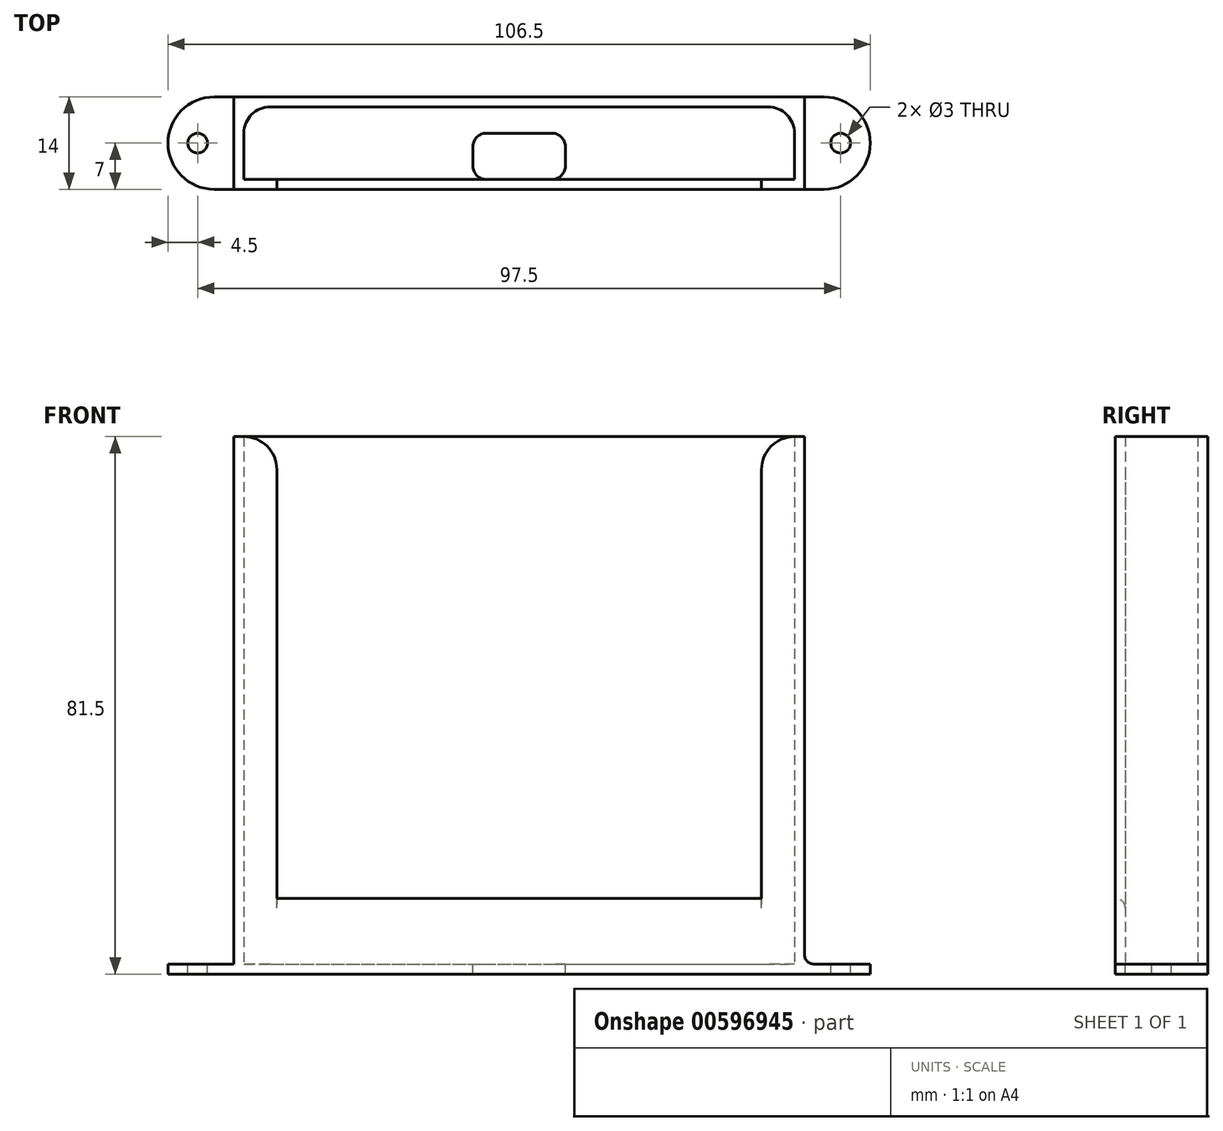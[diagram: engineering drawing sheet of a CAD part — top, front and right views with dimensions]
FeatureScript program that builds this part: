
annotation { "Feature Type Name" : "Feature", "Feature Type Description" : "" }
export const myFeature = defineFeature(function(context is Context, id is Id, definition is map)
    precondition{}
    {
        {
            assignVariable(context, id + "F0", {"name" : "THK", "anyValue" : 1.5});
        }
        {
            var Q0;
            Q0=qCreatedBy(makeId("Top.planeOp"),FACE);
            var sketch = newSketch(context, id + "F1", { "sketchPlane" : qUnion([Q0])});
            skLineSegment(sketch, "E0.bottom", {"start": v(-85, -1.5) * mm, "end": v(-1.5, -1.5) * mm});
            skLineSegment(sketch, "E0.top", {"start": v(-85, -12.5) * mm, "end": v(-1.5, -12.5) * mm});
            skLineSegment(sketch, "E0.left", {"start": v(-85, -1.5) * mm, "end": v(-85, -12.5) * mm});
            skLineSegment(sketch, "E0.right", {"start": v(-1.5, -1.5) * mm, "end": v(-1.5, -12.5) * mm});
            skLineSegment(sketch, "E1.0", {"start": v(-86.5, 0) * mm, "end": v(0, 0) * mm});
            skLineSegment(sketch, "E1.1", {"start": v(-86.5, 0) * mm, "end": v(-86.5, -14) * mm});
            skLineSegment(sketch, "E1.2", {"start": v(-86.5, -14) * mm, "end": v(0, -14) * mm});
            skLineSegment(sketch, "E1.3", {"start": v(0, 0) * mm, "end": v(0, -14) * mm});
            skLineSegment(sketch, "E2", {"start": v(-1.5, -12.5) * mm, "end": v(0, -12.5) * mm});
            skLineSegment(sketch, "E3", {"start": v(-85, -12.5) * mm, "end": v(-86.5, -12.5) * mm});
            skLineSegment(sketch, "E4", {"start": v(-43.25, -1.5) * mm, "end": v(-43.25, -12.5) * mm, "construction": true});
            skLineSegment(sketch, "E5", {"start": v(-86.5, 0) * mm, "end": v(-89.5, 0) * mm});
            skLineSegment(sketch, "E6", {"start": v(0, 0) * mm, "end": v(3, 0) * mm});
            skLineSegment(sketch, "E7", {"start": v(0, -14) * mm, "end": v(3, -14) * mm});
            skLineSegment(sketch, "E8", {"start": v(-86.5, -14) * mm, "end": v(-89.5, -14) * mm});
            skArc(sketch, "E9", {"start": v(-89.5, 0) * mm, "mid": v(-96.5, -7) * mm, "end": v(-89.5, -14) * mm});
            skArc(sketch, "E10", {"start": v(3, 0) * mm, "mid": v(10, -7) * mm, "end": v(3, -14) * mm});
            skLineSegment(sketch, "E11", {"start": v(-96.5, -7) * mm, "end": v(10, -7) * mm, "construction": true});
            skCircle(sketch, "E12", {"center": v(-92, -7) * mm, "radius": 1.5 * mm});
            skCircle(sketch, "E13.MirrorC", {"center": v(5.5, -7) * mm, "radius": 1.5 * mm});
            skLineSegment(sketch, "E14", {"start": v(-6.5, -12.5) * mm, "end": v(-6.5, -14) * mm});
            skLineSegment(sketch, "E15", {"start": v(-80, -12.5) * mm, "end": v(-80, -14) * mm});
            skLineSegment(sketch, "E16", {"start": v(-48.25, -5.5) * mm, "end": v(-38.25, -5.5) * mm});
            skLineSegment(sketch, "E17", {"start": v(-38.25, -12.5) * mm, "end": v(-48.25, -12.5) * mm});
            skPoint(sketch, "E18", {"position": v(-43.25, -5.5) * mm});
            skLineSegment(sketch, "E19", {"start": v(-50.25, -7.5) * mm, "end": v(-50.25, -10.5) * mm});
            skLineSegment(sketch, "E20", {"start": v(-36.25, -7.5) * mm, "end": v(-36.25, -10.5) * mm});
            skPoint(sketch, "E21.visualSharp", {"position": v(-50.25, -5.5) * mm});
            skArc(sketch, "E21.filletArc", {"start": v(-48.25, -5.5) * mm, "mid": v(-49.66, -6.09) * mm, "end": v(-50.25, -7.5) * mm});
            skPoint(sketch, "E22.visualSharp", {"position": v(-50.25, -12.5) * mm});
            skArc(sketch, "E22.filletArc", {"start": v(-50.25, -10.5) * mm, "mid": v(-49.66, -11.91) * mm, "end": v(-48.25, -12.5) * mm});
            skPoint(sketch, "E23.visualSharp", {"position": v(-36.25, -12.5) * mm});
            skArc(sketch, "E23.filletArc", {"start": v(-38.25, -12.5) * mm, "mid": v(-36.84, -11.91) * mm, "end": v(-36.25, -10.5) * mm});
            skPoint(sketch, "E24.visualSharp", {"position": v(-36.25, -5.5) * mm});
            skArc(sketch, "E24.filletArc", {"start": v(-36.25, -7.5) * mm, "mid": v(-36.84, -6.09) * mm, "end": v(-38.25, -5.5) * mm});
            skSolve(sketch);
        }
        {
            var Q0;
            Q0=makeQuery(id+"F1.imprint","IMPRINT",FACE,{"disambiguationData":[TD([[makeQuery(id+"F1.imprint","IMPRINT",EDGE,{"derivedFrom":sQuery(id+"F1.wireOp",EDGE,"E0.right")}),1.0]])]});
            var Q1;
            Q1=makeQuery(id+"F1.imprint","IMPRINT",FACE,{"disambiguationData":[TD([[makeQuery(id+"F1.imprint","IMPRINT",EDGE,{"derivedFrom":sQuery(id+"F1.wireOp",EDGE,"E0.top")}),-1.0]])]});
            var Q2;
            Q2=makeQuery(id+"F1.imprint","IMPRINT",FACE,{"disambiguationData":[TD([[makeQuery(id+"F1.imprint","IMPRINT",EDGE,{"derivedFrom":sQuery(id+"F1.wireOp",EDGE,"E0.bottom")}),1.0]])]});
            var Q3;
            Q3=makeQuery(id+"F1.imprint","IMPRINT",FACE,{"disambiguationData":[TD([[makeQuery(id+"F1.imprint","IMPRINT",EDGE,{"derivedFrom":sQuery(id+"F1.wireOp",EDGE,"E0.bottom")}),-1.0]])]});
            var Q4;
            {var subQ0=sQuery(id+"F1.wireOp",EDGE,"v1pQhFt7-J4Kf-ouM1-Mokq-JOx43GeG9Wj8");Q4=makeQuery(id+"F1.imprint","IMPRINT",FACE,{"disambiguationData":[TD([[makeQuery(id+"F1.imprint","IMPRINT",EDGE,{"derivedFrom":subQ0}),1.0]])]});}
            var Q5;
            {var subQ0=sQuery(id+"F1.wireOp",EDGE,"f7334b1f-d61c-490d-bf83-d8ae5c5b7b340.MirrorCS");Q5=makeQuery(id+"F1.imprint","IMPRINT",FACE,{"disambiguationData":[TD([[makeQuery(id+"F1.imprint","IMPRINT",EDGE,{"derivedFrom":subQ0}),-1.0]])]});}
            var Q6;
            {var subQ3=sQuery(id+"F1.wireOp",EDGE,"E5");Q6=makeQuery(id+"F1.imprint","IMPRINT",FACE,{"disambiguationData":[TD([[makeQuery(id+"F1.imprint","IMPRINT",EDGE,{"derivedFrom":subQ3}),1.0]])]});}
            var Q7;
            {var subQ0=sQuery(id+"F1.wireOp",EDGE,"E6");Q7=makeQuery(id+"F1.imprint","IMPRINT",FACE,{"disambiguationData":[TD([[makeQuery(id+"F1.imprint","IMPRINT",EDGE,{"derivedFrom":subQ0}),-1.0]])]});}
            var Q8;
            {var subQ0=sQuery(id+"F1.wireOp",EDGE,"E3");Q8=makeQuery(id+"F1.imprint","IMPRINT",FACE,{"disambiguationData":[TD([[makeQuery(id+"F1.imprint","IMPRINT",EDGE,{"derivedFrom":subQ0}),1.0]])]});}
            var Q9;
            {var subQ0=sQuery(id+"F1.wireOp",EDGE,"E2");Q9=makeQuery(id+"F1.imprint","IMPRINT",FACE,{"disambiguationData":[TD([[makeQuery(id+"F1.imprint","IMPRINT",EDGE,{"derivedFrom":subQ0}),-1.0]])]});}
            extrude(context, id + "F2", {"entities" : qUnion([Q0, Q1, Q2, Q3, Q4, Q5, Q6, Q7, Q8, Q9]), "oppositeDirection" : true, "depth" : (getVariable(context, 'THK')) * mm, "offsetDistance" : 25 * mm});
        }
        {
            var Q0;
            {var subQ0=sQuery(id+"F1.wireOp",EDGE,"E2");Q0=makeQuery(id+"F1.imprint","IMPRINT",FACE,{"disambiguationData":[TD([[makeQuery(id+"F1.imprint","IMPRINT",EDGE,{"derivedFrom":subQ0}),-1.0]])]});}
            var Q1;
            {var subQ0=sQuery(id+"F1.wireOp",EDGE,"E3");Q1=makeQuery(id+"F1.imprint","IMPRINT",FACE,{"disambiguationData":[TD([[makeQuery(id+"F1.imprint","IMPRINT",EDGE,{"derivedFrom":subQ0}),1.0]])]});}
            var Q2;
            {var subQ0=sQuery(id+"F1.wireOp",EDGE,"E14");Q2=makeQuery(id+"F1.imprint","IMPRINT",FACE,{"disambiguationData":[TD([[makeQuery(id+"F1.imprint","IMPRINT",EDGE,{"derivedFrom":subQ0}),-1.0]])]});}
            extrude(context, id + "F3", {"entities" : qUnion([Q0, Q1, Q2]), "operationType" : NewBodyOperationType.ADD, "depth" : 10 * mm, "offsetDistance" : 25 * mm});
        }
        {
            var Q0;
            Q0=makeQuery(id+"F1.imprint","IMPRINT",FACE,{"disambiguationData":[TD([[makeQuery(id+"F1.imprint","IMPRINT",EDGE,{"derivedFrom":sQuery(id+"F1.wireOp",EDGE,"E0.right")}),1.0]])]});
            var Q1;
            {var subQ0=sQuery(id+"F1.wireOp",EDGE,"E3");Q1=makeQuery(id+"F1.imprint","IMPRINT",FACE,{"disambiguationData":[TD([[makeQuery(id+"F1.imprint","IMPRINT",EDGE,{"derivedFrom":subQ0}),1.0]])]});}
            var Q2;
            {var subQ0=sQuery(id+"F1.wireOp",EDGE,"E2");Q2=makeQuery(id+"F1.imprint","IMPRINT",FACE,{"disambiguationData":[TD([[makeQuery(id+"F1.imprint","IMPRINT",EDGE,{"derivedFrom":subQ0}),-1.0]])]});}
            extrude(context, id + "F4", {"entities" : qUnion([Q0, Q1, Q2]), "operationType" : NewBodyOperationType.ADD, "depth" : 80 * mm, "offsetDistance" : 25 * mm});
        }
        {
            var Q0;
            Q0=makeQuery(id+"F4.opExtrude","CAP_EDGE",EDGE,{"disambiguationData":[OSD([sQuery(id+"F1.wireOp",EDGE,"E15")])],"isStart":false});
            var Q1;
            Q1=makeQuery(id+"F4.opExtrude","CAP_EDGE",EDGE,{"disambiguationData":[OSD([sQuery(id+"F1.wireOp",EDGE,"E14")])],"isStart":false});
            fillet(context, id + "F5", {"entities" : qUnion([Q0, Q1]), "radius" : 5 * mm, "tangentPropagation" : true, "allowEdgeOverflow" : false});
        }
        {
            var Q0;
            {var subQ0=sQuery(id+"F1.wireOp",EDGE,"E3");var subQ1=sQuery(id+"F1.wireOp",EDGE,"E0.top");Q0=makeQuery(id+"F4.boolean.opBoolean","SPLIT",EDGE,{"disambiguationData":[topologyDisambiguationEdgeConnected([makeQuery(id+"F4.opExtrude","SWEPT_FACE",FACE,{"disambiguationData":[OSD([subQ0])]})])],"derivedFrom":makeQuery(id+"F3.opExtrude","CAP_EDGE",EDGE,{"disambiguationData":[OSD([subQ1,subQ0])],"isStart":false})});}
            var Q1;
            {var subQ0=sQuery(id+"F1.wireOp",EDGE,"E1.1");Q1=makeQuery(id+"F4.boolean.opBoolean","MERGE",EDGE,{"derivedFrom":[makeQuery(id+"F3.opExtrude","CAP_EDGE",EDGE,{"disambiguationData":[OSD([subQ0])],"isStart":true}),makeQuery(id+"F4.opExtrude","CAP_EDGE",EDGE,{"disambiguationData":[OSD([subQ0])],"isStart":true})]});}
            var Q2;
            {var subQ0=sQuery(id+"F1.wireOp",EDGE,"E2");var subQ1=sQuery(id+"F1.wireOp",EDGE,"E0.top");Q2=makeQuery(id+"F4.boolean.opBoolean","SPLIT",EDGE,{"disambiguationData":[topologyDisambiguationEdgeConnected([makeQuery(id+"F4.opExtrude","SWEPT_FACE",FACE,{"disambiguationData":[OSD([subQ0])]})])],"derivedFrom":makeQuery(id+"F3.opExtrude","CAP_EDGE",EDGE,{"disambiguationData":[OSD([subQ1,subQ0])],"isStart":false})});}
            var Q3;
            {var subQ0=sQuery(id+"F1.wireOp",EDGE,"E1.3");Q3=makeQuery(id+"F4.boolean.opBoolean","MERGE",EDGE,{"derivedFrom":[makeQuery(id+"F3.opExtrude","CAP_EDGE",EDGE,{"disambiguationData":[OSD([subQ0])],"isStart":true}),makeQuery(id+"F4.opExtrude","CAP_EDGE",EDGE,{"disambiguationData":[OSD([subQ0])],"isStart":true})]});}
            fillet(context, id + "F6", {"entities" : qUnion([Q0, Q1, Q2, Q3]), "radius" : (getVariable(context, 'THK')) * mm, "tangentPropagation" : true, "allowEdgeOverflow" : false});
        }
        {
            var Q0;
            Q0=makeQuery(id+"F4.opExtrude","SWEPT_EDGE",EDGE,{"disambiguationData":[OSD([sQuery(id+"F1.wireOp",EDGE,"E0.bottom"),sQuery(id+"F1.wireOp",EDGE,"E0.left")])]});
            var Q1;
            Q1=makeQuery(id+"F4.opExtrude","SWEPT_EDGE",EDGE,{"disambiguationData":[OSD([sQuery(id+"F1.wireOp",EDGE,"E0.bottom"),sQuery(id+"F1.wireOp",EDGE,"E0.right")])]});
            fillet(context, id + "F7", {"entities" : qUnion([Q0, Q1]), "radius" : 4 * mm, "tangentPropagation" : true, "allowEdgeOverflow" : false});
        }
    });
